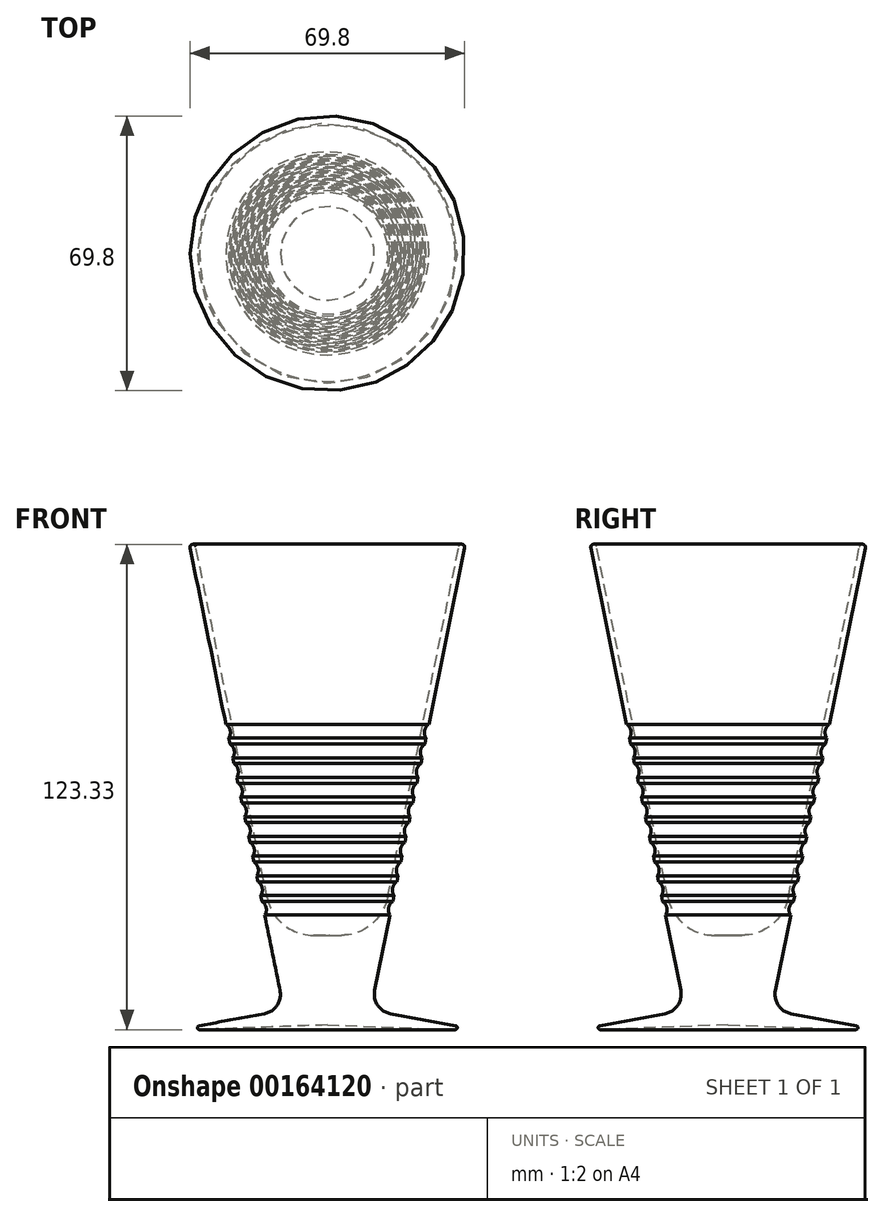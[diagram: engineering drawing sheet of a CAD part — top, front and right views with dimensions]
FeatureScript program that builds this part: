
annotation { "Feature Type Name" : "Feature", "Feature Type Description" : "" }
export const myFeature = defineFeature(function(context is Context, id is Id, definition is map)
    precondition{}
    {
        {
            var Q0;
            Q0=qCreatedBy(makeId("Front.planeOp"),FACE);
            var sketch = newSketch(context, id + "F0", { "sketchPlane" : qUnion([Q0])});
            skLineSegment(sketch, "E0", {"start": v(12.02, 9.96) * mm, "end": v(15.91, 29.1) * mm});
            skLineSegment(sketch, "E1", {"start": v(0, 1.2) * mm, "end": v(0, 24) * mm});
            skPoint(sketch, "E2.endSnap0", {"position": v(5, 0) * mm});
            skLineSegment(sketch, "E3", {"start": v(32.6, 1) * mm, "end": v(16.02, 4.05) * mm});
            skLineSegment(sketch, "E4", {"start": v(0, 24) * mm, "end": v(0.48, 24) * mm});
            skLineSegment(sketch, "E5.0", {"start": v(15.3, 33.6) * mm, "end": v(33.42, 122.73) * mm});
            skArc(sketch, "E6", {"start": v(34.89, 122.43) * mm, "mid": v(34.3, 123.32) * mm, "end": v(33.42, 122.73) * mm});
            skPoint(sketch, "E7.orphan", {"position": v(35, 123) * mm});
            skLineSegment(sketch, "E8", {"start": v(0.52, 24) * mm, "end": v(3.5, 24) * mm});
            skPoint(sketch, "E9.visualSharp", {"position": v(13.34, 23.96) * mm});
            skArc(sketch, "E9.filletArc", {"start": v(3.5, 24) * mm, "mid": v(11.12, 26.69) * mm, "end": v(15.3, 33.6) * mm});
            skPoint(sketch, "E10.visualSharp", {"position": v(0.5, 24) * mm});
            skArc(sketch, "E10.filletArc", {"start": v(0.52, 24) * mm, "mid": v(0.5, 24) * mm, "end": v(0.48, 24) * mm});
            skPoint(sketch, "E11.orphan", {"position": v(0, 7) * mm});
            skArc(sketch, "E12", {"start": v(32.5, 0) * mm, "mid": v(33, 0.45) * mm, "end": v(32.6, 1) * mm});
            skPoint(sketch, "E13.orphan", {"position": v(37.97, 0) * mm});
            skPoint(sketch, "E14.visualSharp", {"position": v(11.01, 4.97) * mm});
            skArc(sketch, "E14.filletArc", {"start": v(12.02, 9.96) * mm, "mid": v(12.78, 6.17) * mm, "end": v(16.02, 4.05) * mm});
            skLineSegment(sketch, "E15", {"start": v(0, 1.2) * mm, "end": v(32.5, 0) * mm});
            skArc(sketch, "E16", {"start": v(16.63, 32.6) * mm, "mid": v(15.54, 31) * mm, "end": v(15.91, 29.1) * mm});
            skArc(sketch, "E17", {"start": v(18.66, 42.6) * mm, "mid": v(17.57, 41) * mm, "end": v(17.95, 39.1) * mm});
            skArc(sketch, "E18", {"start": v(19.67, 47.6) * mm, "mid": v(18.58, 46) * mm, "end": v(18.96, 44.1) * mm});
            skArc(sketch, "E19", {"start": v(20.7, 52.6) * mm, "mid": v(19.6, 51) * mm, "end": v(19.98, 49.1) * mm});
            skArc(sketch, "E20", {"start": v(21.7, 57.6) * mm, "mid": v(20.62, 56) * mm, "end": v(21, 54.1) * mm});
            skArc(sketch, "E21", {"start": v(24.76, 72.6) * mm, "mid": v(23.67, 71) * mm, "end": v(24.04, 69.1) * mm});
            skArc(sketch, "E22", {"start": v(25.77, 77.6) * mm, "mid": v(24.68, 76) * mm, "end": v(25.06, 74.1) * mm});
            skLineSegment(sketch, "E23.trimOffspring", {"start": v(16.63, 32.6) * mm, "end": v(16.93, 34.1) * mm});
            skLineSegment(sketch, "E24.trimOffspring", {"start": v(17.64, 37.6) * mm, "end": v(17.95, 39.1) * mm});
            skArc(sketch, "E25.trimOffspring", {"start": v(17.64, 37.6) * mm, "mid": v(16.55, 36) * mm, "end": v(16.93, 34.1) * mm});
            skLineSegment(sketch, "E26.trimOffspring", {"start": v(18.66, 42.6) * mm, "end": v(18.96, 44.1) * mm});
            skLineSegment(sketch, "E27.trimOffspring", {"start": v(19.67, 47.6) * mm, "end": v(19.98, 49.1) * mm});
            skLineSegment(sketch, "E28.trimOffspring", {"start": v(20.7, 52.6) * mm, "end": v(21, 54.1) * mm});
            skLineSegment(sketch, "E29.trimOffspring", {"start": v(21.7, 57.6) * mm, "end": v(22.01, 59.1) * mm});
            skArc(sketch, "E30.trimOffspring", {"start": v(22.72, 62.6) * mm, "mid": v(21.63, 61) * mm, "end": v(22.01, 59.1) * mm});
            skLineSegment(sketch, "E31.trimOffspring", {"start": v(22.72, 62.6) * mm, "end": v(23.03, 64.1) * mm});
            skLineSegment(sketch, "E32.trimOffspring", {"start": v(23.74, 67.6) * mm, "end": v(24.04, 69.1) * mm});
            skArc(sketch, "E33.trimOffspring", {"start": v(23.74, 67.6) * mm, "mid": v(22.65, 66) * mm, "end": v(23.03, 64.1) * mm});
            skLineSegment(sketch, "E34.trimOffspring", {"start": v(24.76, 72.6) * mm, "end": v(25.06, 74.1) * mm});
            skLineSegment(sketch, "E35.trimOffspring", {"start": v(25.77, 77.6) * mm, "end": v(34.89, 122.43) * mm});
            skSolve(sketch);
        }
        {
            var Q0;
            Q0=makeQuery(id+"F0.imprint","IMPRINT",FACE,{"disambiguationData":[TD([[makeQuery(id+"F0.imprint","IMPRINT",EDGE,{"derivedFrom":sQuery(id+"F0.wireOp",EDGE,"E0")}),1.0]])]});
            var Q1;
            Q1=sQuery(id+"F0.wireOp",EDGE,"E1");
            revolve(context, id + "F1", {"entities" : qUnion([Q0]), "axis" : qUnion([Q1]), "revolveType" : RevolveType.FULL});
        }
    });
